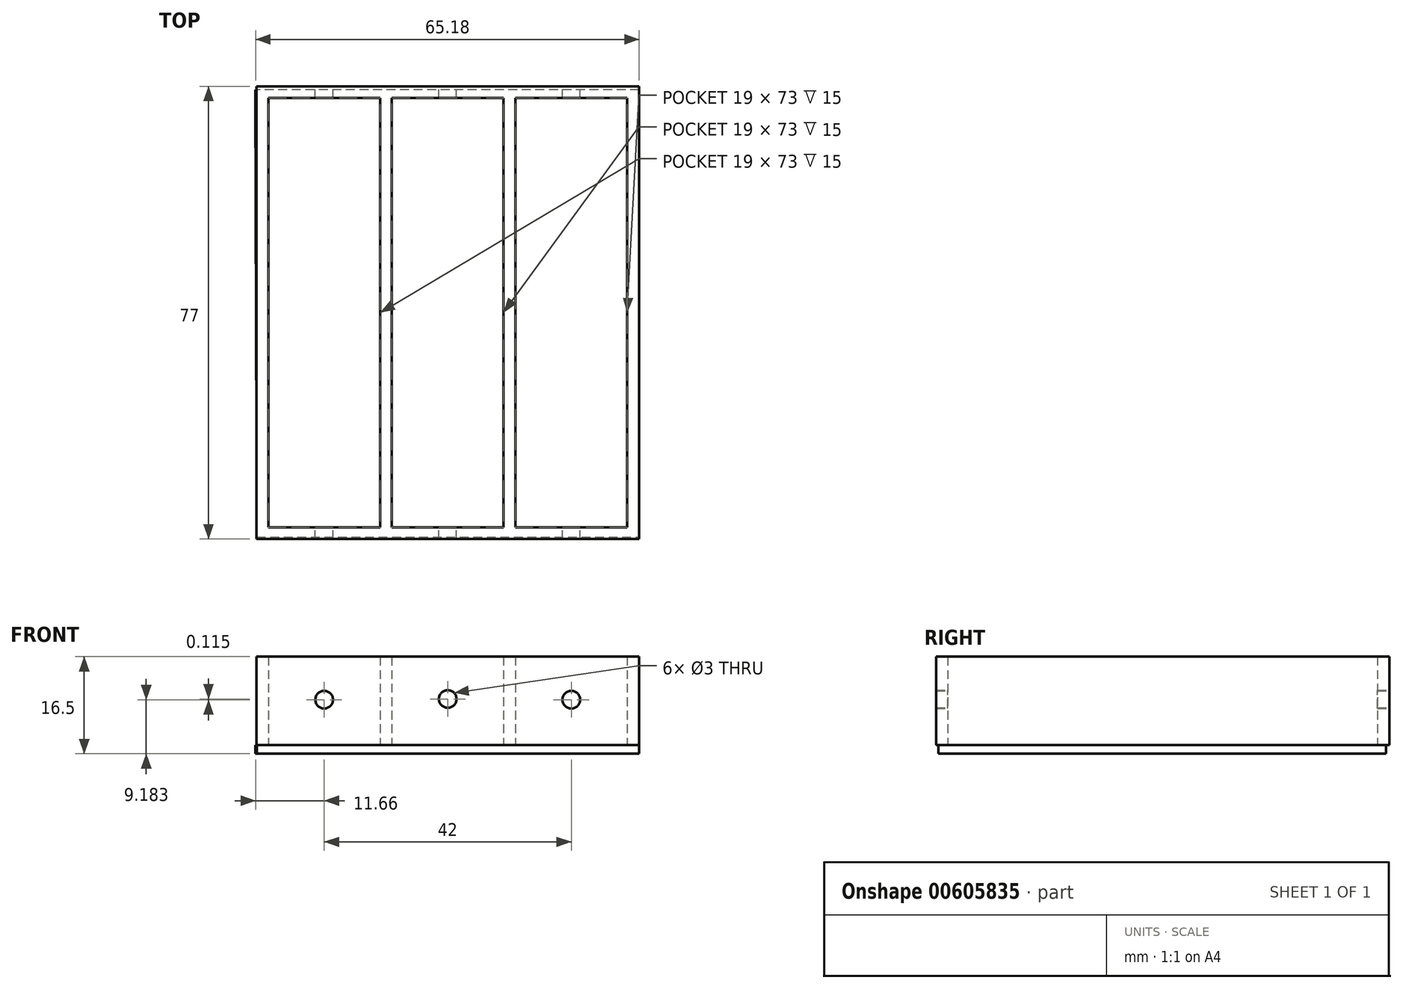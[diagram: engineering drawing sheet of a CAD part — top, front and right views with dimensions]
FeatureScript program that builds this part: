
annotation { "Feature Type Name" : "Feature", "Feature Type Description" : "" }
export const myFeature = defineFeature(function(context is Context, id is Id, definition is map)
    precondition{}
    {
        {
            var Q0;
            Q0=qCreatedBy(makeId("Top.planeOp"),FACE);
            var sketch = newSketch(context, id + "F0", { "sketchPlane" : qUnion([Q0])});
            skLineSegment(sketch, "E0.bottom", {"start": v(32.5, 38.5) * mm, "end": v(-32.5, 38.5) * mm});
            skLineSegment(sketch, "E0.top", {"start": v(32.5, -38.5) * mm, "end": v(-32.5, -38.5) * mm});
            skLineSegment(sketch, "E0.left", {"start": v(32.5, 38.5) * mm, "end": v(32.5, -38.5) * mm});
            skLineSegment(sketch, "E0.right", {"start": v(-32.5, 38.5) * mm, "end": v(-32.5, -38.5) * mm});
            skPoint(sketch, "E0.middle", {"position": v(0, 0) * mm});
            skLineSegment(sketch, "E1.0", {"start": v(30.5, 36.5) * mm, "end": v(-30.5, 36.5) * mm});
            skLineSegment(sketch, "E1.1", {"start": v(30.5, 36.5) * mm, "end": v(30.5, -36.5) * mm});
            skLineSegment(sketch, "E1.2", {"start": v(30.5, -36.5) * mm, "end": v(-30.5, -36.5) * mm});
            skLineSegment(sketch, "E1.3", {"start": v(-30.5, 36.5) * mm, "end": v(-30.5, -36.5) * mm});
            skLineSegment(sketch, "E2", {"start": v(-11.5, 36.5) * mm, "end": v(-11.5, -36.5) * mm});
            skLineSegment(sketch, "E3", {"start": v(11.5, 36.5) * mm, "end": v(11.5, -36.5) * mm});
            skLineSegment(sketch, "E4", {"start": v(-9.5, 36.5) * mm, "end": v(-9.5, -36.5) * mm});
            skLineSegment(sketch, "E5", {"start": v(9.5, 36.5) * mm, "end": v(9.5, -36.5) * mm});
            skSolve(sketch);
        }
        {
            var Q0;
            Q0 = qSketchRegion(id + "F0", true);
            var Q1;
            {var subQ0=sQuery(id+"F0.wireOp",EDGE,"E2");Q1=makeQuery(id+"F0.imprint","IMPRINT",FACE,{"disambiguationData":[TD([[makeQuery(id+"F0.imprint","IMPRINT",EDGE,{"derivedFrom":subQ0}),1.0]])]});}
            var Q2;
            {var subQ0=sQuery(id+"F0.wireOp",EDGE,"E3");Q2=makeQuery(id+"F0.imprint","IMPRINT",FACE,{"disambiguationData":[TD([[makeQuery(id+"F0.imprint","IMPRINT",EDGE,{"derivedFrom":subQ0}),-1.0]])]});}
            extrude(context, id + "F1", {"entities" : qUnion([Q0, Q1, Q2]), "depth" : 15 * mm, "offsetDistance" : 25 * mm});
        }
        {
            var Q0;
            Q0=qCreatedBy(makeId("Top.planeOp"),FACE);
            var sketch = newSketch(context, id + "F2", { "sketchPlane" : qUnion([Q0])});
            skLineSegment(sketch, "E6", {"start": v(-32.45, -38.15) * mm, "end": v(32.52, -38.15) * mm});
            skLineSegment(sketch, "E7", {"start": v(32.52, -38.15) * mm, "end": v(32.52, 37.94) * mm});
            skLineSegment(sketch, "E8", {"start": v(32.52, 37.94) * mm, "end": v(-32.66, 37.94) * mm});
            skLineSegment(sketch, "E9", {"start": v(-32.66, 37.94) * mm, "end": v(-32.45, -38.15) * mm});
            skSolve(sketch);
        }
        {
            var Q0;
            Q0 = qSketchRegion(id + "F2", true);
            extrude(context, id + "F3", {"entities" : qUnion([Q0]), "operationType" : NewBodyOperationType.ADD, "depth" : -1.5 * mm, "offsetDistance" : 25 * mm});
        }
        {
            var Q0;
            Q0=makeQuery(id+"F1.opExtrude","SWEPT_FACE",FACE,{"disambiguationData":[OSD([sQuery(id+"F0.wireOp",EDGE,"E0.bottom")])]});
            var sketch = newSketch(context, id + "F4", { "sketchPlane" : qUnion([Q0])});
            skLineSegment(sketch, "E10", {"start": v(-32.5, 7.5) * mm, "end": v(32.5, 7.5) * mm, "construction": true});
            skSolve(sketch);
        }
        {
            var Q0;
            {var subQ0=sQuery(id+"F0.wireOp",EDGE,"E0.bottom");Q0=makeQuery(id+"F4.imprint","IMPRINT",FACE,{"disambiguationData":[TD([[makeQuery(id+"F4.imprint","IMPRINT",EDGE,{"derivedFrom":makeQuery(id+"F1.opExtrude","CAP_EDGE",EDGE,{"disambiguationData":[OSD([subQ0])],"isStart":true})}),1.0]])]});}
            var sketch = newSketch(context, id + "F5", { "sketchPlane" : qUnion([Q0])});
            skCircle(sketch, "E11", {"center": v(-21, 7.68) * mm, "radius": 1.5 * mm});
            skCircle(sketch, "E12", {"center": v(0, 7.8) * mm, "radius": 1.5 * mm});
            skCircle(sketch, "E13.MirrorC", {"center": v(21, 7.68) * mm, "radius": 1.5 * mm});
            skSolve(sketch);
        }
        {
            var Q0;
            Q0 = qSketchRegion(id + "F5", true);
            extrude(context, id + "F6", {"entities" : qUnion([Q0]), "operationType" : NewBodyOperationType.REMOVE, "oppositeDirection" : true, "depth" : 80 * mm, "offsetDistance" : 25 * mm});
        }
    });
